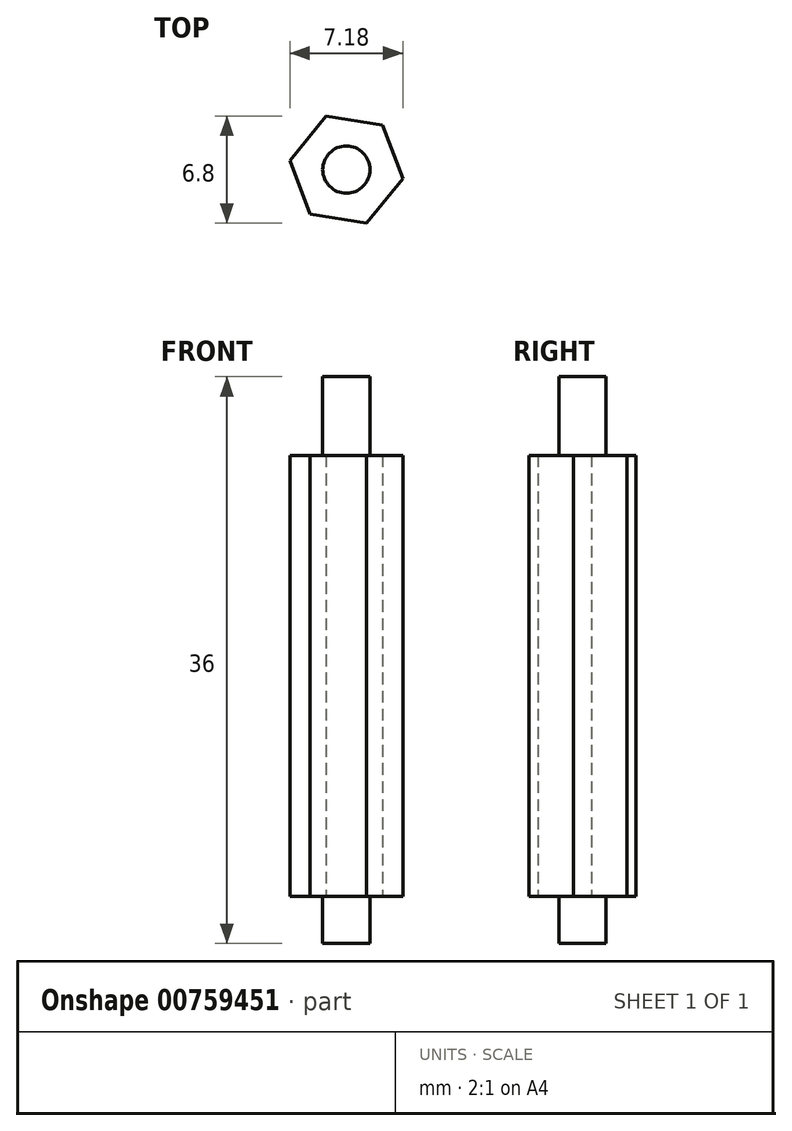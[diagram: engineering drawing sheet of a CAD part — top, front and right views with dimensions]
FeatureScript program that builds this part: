
annotation { "Feature Type Name" : "Feature", "Feature Type Description" : "" }
export const myFeature = defineFeature(function(context is Context, id is Id, definition is map)
    precondition{}
    {
        {
            var Q0;
            Q0=qCreatedBy(makeId("Top.planeOp"),FACE);
            var sketch = newSketch(context, id + "F0", { "sketchPlane" : qUnion([Q0])});
            skCircle(sketch, "E0.cCircle", {"center": v(0, 0) * mm, "radius": 3.15 * mm, "construction": true});
            skLineSegment(sketch, "E0.0", {"start": v(2.3, 2.82) * mm, "end": v(3.6, -0.58) * mm});
            skLineSegment(sketch, "E0.1", {"start": v(3.6, -0.58) * mm, "end": v(1.3, -3.4) * mm});
            skLineSegment(sketch, "E0.2", {"start": v(1.3, -3.4) * mm, "end": v(-2.3, -2.82) * mm});
            skLineSegment(sketch, "E0.3", {"start": v(-2.3, -2.82) * mm, "end": v(-3.6, 0.58) * mm});
            skLineSegment(sketch, "E0.4", {"start": v(-3.6, 0.58) * mm, "end": v(-1.3, 3.4) * mm});
            skLineSegment(sketch, "E0.5", {"start": v(-1.3, 3.4) * mm, "end": v(2.3, 2.82) * mm});
            skPoint(sketch, "E0.0.midPoint", {"position": v(2.94, 1.12) * mm});
            skCircle(sketch, "E1", {"center": v(0, 0) * mm, "radius": 1.5 * mm});
            skSolve(sketch);
        }
        {
            var Q0;
            Q0=makeQuery(id+"F0.imprint","IMPRINT",FACE,{"disambiguationData":[TD([[makeQuery(id+"F0.imprint","IMPRINT",EDGE,{"derivedFrom":sQuery(id+"F0.wireOp",EDGE,"E0.0")}),-1.0]])]});
            extrude(context, id + "F1", {"entities" : qUnion([Q0]), "endBound" : BoundingType.SYMMETRIC, "depth" : 28 * mm, "offsetDistance" : 25 * mm});
        }
        {
            var Q0;
            Q0=makeQuery(id+"F0.imprint","IMPRINT",FACE,{"disambiguationData":[TD([[makeQuery(id+"F0.imprint","IMPRINT",EDGE,{"derivedFrom":sQuery(id+"F0.wireOp",EDGE,"E1")}),1.0]])]});
            extrude(context, id + "F2", {"entities" : qUnion([Q0]), "operationType" : NewBodyOperationType.ADD, "endBound" : BoundingType.SYMMETRIC, "depth" : 28 * mm, "offsetDistance" : 25 * mm});
        }
        {
            var Q0;
            {var subQ0=sQuery(id+"F0.wireOp",EDGE,"E1");Q0=makeQuery(id+"F2.boolean.opBoolean","MERGE",FACE,{"derivedFrom":[makeQuery(id+"F1.opExtrude","CAP_FACE",FACE,{"disambiguationData":[OSD([sQuery(id+"F0.wireOp",EDGE,"E0.0"),sQuery(id+"F0.wireOp",EDGE,"E0.1"),sQuery(id+"F0.wireOp",EDGE,"E0.2"),sQuery(id+"F0.wireOp",EDGE,"E0.3"),sQuery(id+"F0.wireOp",EDGE,"E0.4"),sQuery(id+"F0.wireOp",EDGE,"E0.5"),subQ0])],"isStart":true}),makeQuery(id+"F2.opExtrude","CAP_FACE",FACE,{"disambiguationData":[OSD([subQ0])],"isStart":true})]});}
            var sketch = newSketch(context, id + "F3", { "sketchPlane" : qUnion([Q0])});
            skCircle(sketch, "E2", {"center": v(0, 0) * mm, "radius": 1.5 * mm});
            skSolve(sketch);
        }
        {
            var Q0;
            Q0=makeQuery(id+"F3.imprint","IMPRINT",FACE,{"disambiguationData":[TD([[makeQuery(id+"F3.imprint","IMPRINT",EDGE,{"derivedFrom":sQuery(id+"F3.wireOp",EDGE,"E2")}),1.0]])]});
            extrude(context, id + "F4", {"entities" : qUnion([Q0]), "operationType" : NewBodyOperationType.ADD, "depth" : 3 * mm, "offsetDistance" : 25 * mm});
        }
        {
            var Q0;
            {var subQ0=sQuery(id+"F0.wireOp",EDGE,"E1");Q0=makeQuery(id+"F2.boolean.opBoolean","MERGE",FACE,{"derivedFrom":[makeQuery(id+"F1.opExtrude","CAP_FACE",FACE,{"disambiguationData":[OSD([sQuery(id+"F0.wireOp",EDGE,"E0.0"),sQuery(id+"F0.wireOp",EDGE,"E0.1"),sQuery(id+"F0.wireOp",EDGE,"E0.2"),sQuery(id+"F0.wireOp",EDGE,"E0.3"),sQuery(id+"F0.wireOp",EDGE,"E0.4"),sQuery(id+"F0.wireOp",EDGE,"E0.5"),subQ0])],"isStart":false}),makeQuery(id+"F2.opExtrude","CAP_FACE",FACE,{"disambiguationData":[OSD([subQ0])],"isStart":false})]});}
            var sketch = newSketch(context, id + "F5", { "sketchPlane" : qUnion([Q0])});
            skCircle(sketch, "E3", {"center": v(0, 0) * mm, "radius": 1.5 * mm});
            skSolve(sketch);
        }
        {
            var Q0;
            Q0 = qSketchRegion(id + "F5", true);
            extrude(context, id + "F6", {"entities" : qUnion([Q0]), "operationType" : NewBodyOperationType.ADD, "depth" : 5 * mm, "offsetDistance" : 25 * mm});
        }
    });
